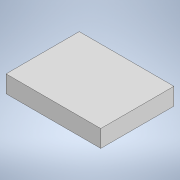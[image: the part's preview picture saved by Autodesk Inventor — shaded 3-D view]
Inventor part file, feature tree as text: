
AUTODESK INVENTOR PART (.ipt)
format: ipt  version: 2021 (Build 250183000, 183)  size: 86,528 bytes
history: native  units: mm
features: extrude x1, sketch x1
ambient origin geometry x8: Origin, YZ Plane, XZ Plane, XY Plane, X Axis, Y Axis, Z Axis, Center Point
bodies: Solid1 (feature_tree)
feature tree (2):
  extrude  "Extrusion1"  Depth=8.0mm
  sketch  "Sketch1"  dims[d0=34.0mm d1=8.0mm d2=44.0mm d3=0.0mm]
